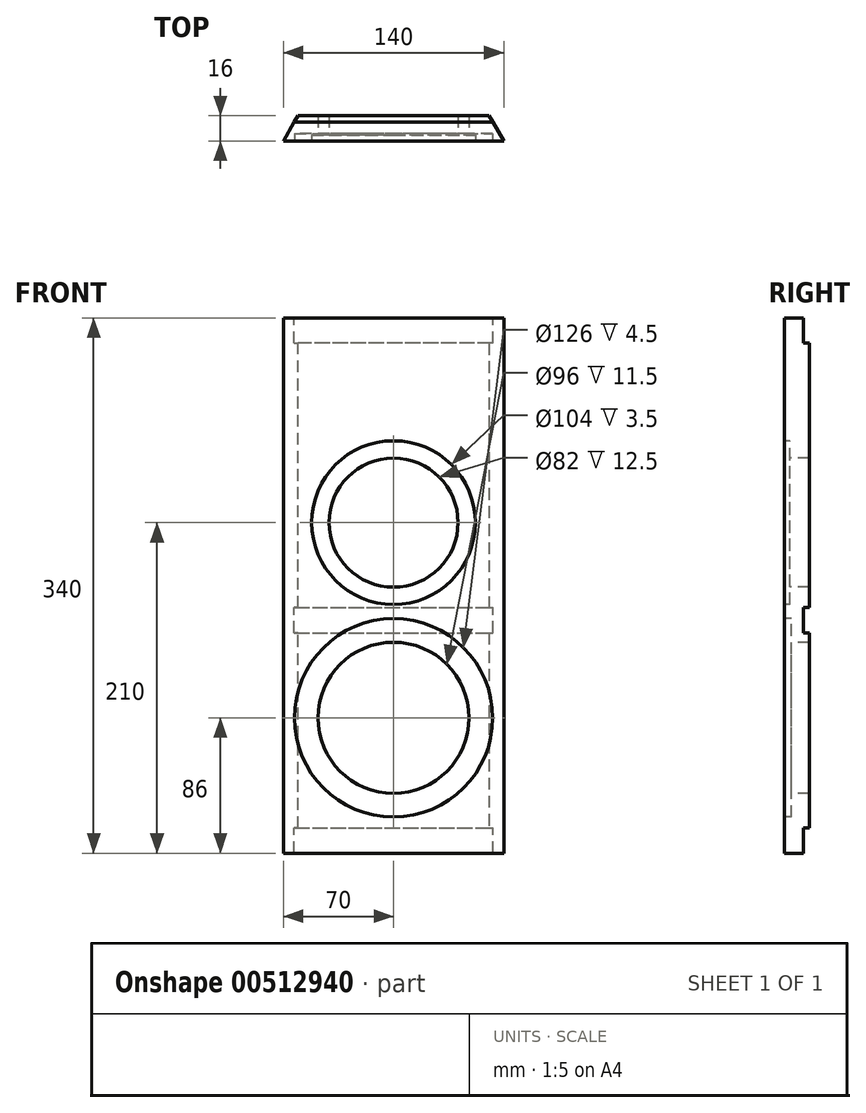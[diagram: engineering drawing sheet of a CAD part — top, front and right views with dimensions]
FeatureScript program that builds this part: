
annotation { "Feature Type Name" : "Feature", "Feature Type Description" : "" }
export const myFeature = defineFeature(function(context is Context, id is Id, definition is map)
    precondition{}
    {
        {
            var Q0;
            Q0=qCreatedBy(makeId("Front.planeOp"),FACE);
            var sketch = newSketch(context, id + "F0", { "sketchPlane" : qUnion([Q0])});
            skLineSegment(sketch, "E0.bottom", {"start": v(70, 170) * mm, "end": v(-70, 170) * mm});
            skLineSegment(sketch, "E0.top", {"start": v(70, -170) * mm, "end": v(-70, -170) * mm});
            skLineSegment(sketch, "E0.left", {"start": v(70, 170) * mm, "end": v(70, -170) * mm});
            skLineSegment(sketch, "E0.right", {"start": v(-70, 170) * mm, "end": v(-70, -170) * mm});
            skPoint(sketch, "E0.middle", {"position": v(0, 0) * mm});
            skSolve(sketch);
        }
        {
            var Q0;
            Q0=makeQuery(id+"F0.imprint","IMPRINT",FACE,{"disambiguationData":[TD([[makeQuery(id+"F0.imprint","IMPRINT",EDGE,{"derivedFrom":sQuery(id+"F0.wireOp",EDGE,"E0.bottom")}),1.0]])]});
            extrude(context, id + "F1", {"entities" : qUnion([Q0]), "depth" : 16 * mm});
        }
        {
            var Q0;
            Q0=makeQuery(id+"F1.opExtrude","CAP_EDGE",EDGE,{"disambiguationData":[OSD([sQuery(id+"F0.wireOp",EDGE,"E0.left")])],"isStart":true});
            chamfer(context, id + "F2", {"entities" : qUnion([Q0]), "chamferType" : ChamferType.OFFSET_ANGLE, "width" : 16 * mm, "oppositeDirection" : true, "angle" : 30 * degree, "tangentPropagation" : true});
        }
        {
            var Q0;
            Q0=makeQuery(id+"F1.opExtrude","CAP_EDGE",EDGE,{"disambiguationData":[OSD([sQuery(id+"F0.wireOp",EDGE,"E0.right")])],"isStart":true});
            chamfer(context, id + "F3", {"entities" : qUnion([Q0]), "chamferType" : ChamferType.OFFSET_ANGLE, "width" : 16 * mm, "oppositeDirection" : false, "angle" : 30 * degree, "tangentPropagation" : true});
        }
        {
            var Q0;
            Q0=makeQuery(id+"F1.opExtrude","CAP_FACE",FACE,{"disambiguationData":[OSD([sQuery(id+"F0.wireOp",EDGE,"E0.bottom"),sQuery(id+"F0.wireOp",EDGE,"E0.top"),sQuery(id+"F0.wireOp",EDGE,"E0.left"),sQuery(id+"F0.wireOp",EDGE,"E0.right")])],"isStart":false});
            var sketch = newSketch(context, id + "F4", { "sketchPlane" : qUnion([Q0])});
            skCircle(sketch, "E1", {"center": v(0, -84) * mm, "radius": 63 * mm});
            skSolve(sketch);
        }
        {
            var Q0;
            Q0=qSketchRegion(id+"F4",true);
            extrude(context, id + "F5", {"entities" : qUnion([Q0]), "operationType" : NewBodyOperationType.REMOVE, "oppositeDirection" : true, "depth" : 4.5 * mm});
        }
        {
            var Q0;
            Q0=makeQuery(id+"F5.boolean.opBoolean","COPY",FACE,{"derivedFrom":makeQuery(id+"F5.opExtrude","CAP_FACE",FACE,{"disambiguationData":[OSD([sQuery(id+"F4.wireOp",EDGE,"E1")])],"isStart":false})});
            var sketch = newSketch(context, id + "F6", { "sketchPlane" : qUnion([Q0])});
            skCircle(sketch, "E2", {"center": v(0, -84) * mm, "radius": 48 * mm});
            skSolve(sketch);
        }
        {
            var Q0;
            Q0=qSketchRegion(id+"F6",true);
            extrude(context, id + "F7", {"entities" : qUnion([Q0]), "operationType" : NewBodyOperationType.REMOVE, "endBound" : BoundingType.THROUGH_ALL, "oppositeDirection" : true, "depth" : 25 * mm});
        }
        {
            var Q0;
            Q0=makeQuery(id+"F1.opExtrude","CAP_FACE",FACE,{"disambiguationData":[OSD([sQuery(id+"F0.wireOp",EDGE,"E0.bottom"),sQuery(id+"F0.wireOp",EDGE,"E0.top"),sQuery(id+"F0.wireOp",EDGE,"E0.left"),sQuery(id+"F0.wireOp",EDGE,"E0.right")])],"isStart":true});
            var sketch = newSketch(context, id + "F8", { "sketchPlane" : qUnion([Q0])});
            skLineSegment(sketch, "E3.bottom", {"start": v(-93.55, 170) * mm, "end": v(80.05, 170) * mm});
            skLineSegment(sketch, "E3.top", {"start": v(-93.55, 154) * mm, "end": v(80.05, 154) * mm});
            skLineSegment(sketch, "E3.left", {"start": v(-93.55, 170) * mm, "end": v(-93.55, 154) * mm});
            skLineSegment(sketch, "E3.right", {"start": v(80.05, 170) * mm, "end": v(80.05, 154) * mm});
            skLineSegment(sketch, "E4.bottom", {"start": v(101.74, -170) * mm, "end": v(-98.55, -170) * mm});
            skLineSegment(sketch, "E4.top", {"start": v(101.74, -154) * mm, "end": v(-98.55, -154) * mm});
            skLineSegment(sketch, "E4.left", {"start": v(101.74, -170) * mm, "end": v(101.74, -154) * mm});
            skLineSegment(sketch, "E4.right", {"start": v(-98.55, -170) * mm, "end": v(-98.55, -154) * mm});
            skLineSegment(sketch, "E5.bottom", {"start": v(103.48, -30) * mm, "end": v(-105.94, -30) * mm});
            skLineSegment(sketch, "E5.top", {"start": v(103.48, -14) * mm, "end": v(-105.94, -14) * mm});
            skLineSegment(sketch, "E5.left", {"start": v(103.48, -30) * mm, "end": v(103.48, -14) * mm});
            skLineSegment(sketch, "E5.right", {"start": v(-105.94, -30) * mm, "end": v(-105.94, -14) * mm});
            skSolve(sketch);
        }
        {
            var Q0;
            Q0=qSketchRegion(id+"F8",true);
            extrude(context, id + "F9", {"entities" : qUnion([Q0]), "operationType" : NewBodyOperationType.REMOVE, "oppositeDirection" : true, "depth" : 4 * mm});
        }
        {
            var Q0;
            Q0=makeQuery(id+"F1.opExtrude","CAP_FACE",FACE,{"disambiguationData":[OSD([sQuery(id+"F0.wireOp",EDGE,"E0.bottom"),sQuery(id+"F0.wireOp",EDGE,"E0.top"),sQuery(id+"F0.wireOp",EDGE,"E0.left"),sQuery(id+"F0.wireOp",EDGE,"E0.right")])],"isStart":false});
            var sketch = newSketch(context, id + "F10", { "sketchPlane" : qUnion([Q0])});
            skCircle(sketch, "E6", {"center": v(0, 40) * mm, "radius": 52 * mm});
            skSolve(sketch);
        }
        {
            var Q0;
            Q0 = qSketchRegion(id + "F10", true);
            extrude(context, id + "F11", {"entities" : qUnion([Q0]), "operationType" : NewBodyOperationType.REMOVE, "oppositeDirection" : true, "offsetDistance" : 25 * mm, "depth" : 3.5 * mm});
        }
        {
            var Q0;
            Q0=makeQuery(id+"F11.boolean.opBoolean","COPY",FACE,{"derivedFrom":makeQuery(id+"F11.opExtrude","CAP_FACE",FACE,{"disambiguationData":[OSD([sQuery(id+"F10.wireOp",EDGE,"E6")])],"isStart":false})});
            var sketch = newSketch(context, id + "F12", { "sketchPlane" : qUnion([Q0])});
            skCircle(sketch, "E7", {"center": v(0, 40) * mm, "radius": 41 * mm});
            skSolve(sketch);
        }
        {
            var Q0;
            Q0 = qSketchRegion(id + "F12", true);
            extrude(context, id + "F13", {"entities" : qUnion([Q0]), "operationType" : NewBodyOperationType.REMOVE, "endBound" : BoundingType.THROUGH_ALL, "oppositeDirection" : true, "depth" : 25 * mm});
        }
    });
